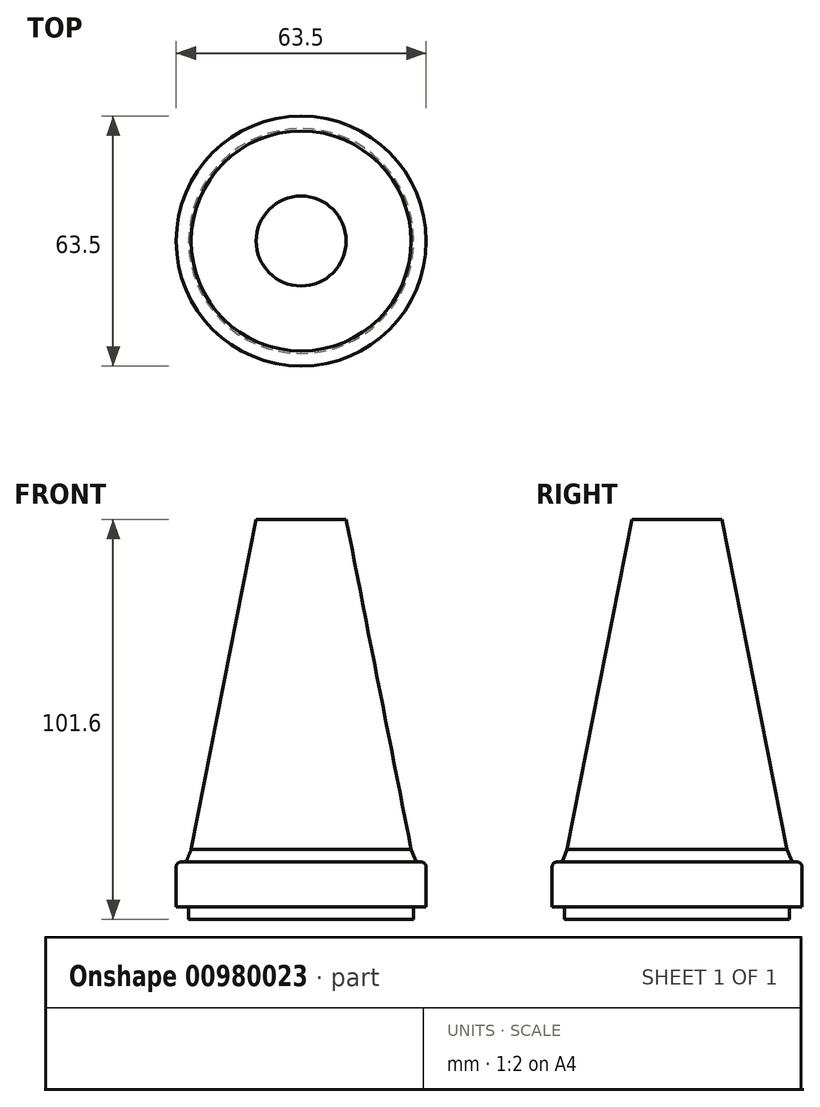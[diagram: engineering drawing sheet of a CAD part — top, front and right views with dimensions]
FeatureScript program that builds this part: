
annotation { "Feature Type Name" : "Feature", "Feature Type Description" : "" }
export const myFeature = defineFeature(function(context is Context, id is Id, definition is map)
    precondition{}
    {
        {
            var Q0;
            Q0=qCreatedBy(makeId("Front.planeOp"),FACE);
            var sketch = newSketch(context, id + "F0", { "sketchPlane" : qUnion([Q0])});
            skLineSegment(sketch, "E0", {"start": v(0, 0) * mm, "end": v(-31.75, 0) * mm});
            skLineSegment(sketch, "E1", {"start": v(-31.75, 0) * mm, "end": v(-31.75, 14.6) * mm});
            skLineSegment(sketch, "E2", {"start": v(-31.75, 14.6) * mm, "end": v(-29.21, 14.6) * mm});
            skLineSegment(sketch, "E3", {"start": v(-11.43, 101.6) * mm, "end": v(0, 101.6) * mm});
            skLineSegment(sketch, "E4", {"start": v(0, 101.6) * mm, "end": v(0, 0) * mm});
            skLineSegment(sketch, "E5", {"start": v(-29.21, 14.6) * mm, "end": v(-27.94, 17.78) * mm});
            skLineSegment(sketch, "E6", {"start": v(-27.94, 17.78) * mm, "end": v(-11.43, 101.6) * mm});
            skLineSegment(sketch, "E7.bottom", {"start": v(-31.75, 0) * mm, "end": v(-28.58, 0) * mm});
            skLineSegment(sketch, "E8", {"start": v(-28.58, 0) * mm, "end": v(-28.58, 3.18) * mm});
            skLineSegment(sketch, "E9", {"start": v(-28.58, 3.18) * mm, "end": v(-31.75, 3.18) * mm});
            skSolve(sketch);
        }
        {
            var Q0;
            {var subQ0=sQuery(id+"F0.wireOp",EDGE,"E2");Q0=makeQuery(id+"F0.imprint","IMPRINT",FACE,{"disambiguationData":[TD([[makeQuery(id+"F0.imprint","IMPRINT",EDGE,{"derivedFrom":subQ0}),-1.0]])]});}
            var Q1;
            Q1=sQuery(id+"F0.wireOp",EDGE,"E4");
            revolve(context, id + "F1", {"surfaceOperationType" : NewSurfaceOperationType.NEW, "entities" : qUnion([Q0]), "axis" : qUnion([Q1]), "revolveType" : RevolveType.FULL});
        }
        {
            var Q0;
            Q0=makeQuery(id+"F1.opRevolve","SWEPT_EDGE",EDGE,{"disambiguationData":[OSD([sQuery(id+"F0.wireOp",EDGE,"E2"),sQuery(id+"F0.wireOp",EDGE,"E5")])]});
            fillet(context, id + "F2", {"entities" : qUnion([Q0]), "radius" : 1.27 * mm, "tangentPropagation" : true, "allowEdgeOverflow" : false});
        }
        {
            var Q0;
            Q0=makeQuery(id+"F1.opRevolve","SWEPT_EDGE",EDGE,{"disambiguationData":[OSD([sQuery(id+"F0.wireOp",EDGE,"E1"),sQuery(id+"F0.wireOp",EDGE,"E2")])]});
            fillet(context, id + "F3", {"entities" : qUnion([Q0]), "radius" : 1.27 * mm, "tangentPropagation" : true, "allowEdgeOverflow" : false});
        }
    });
